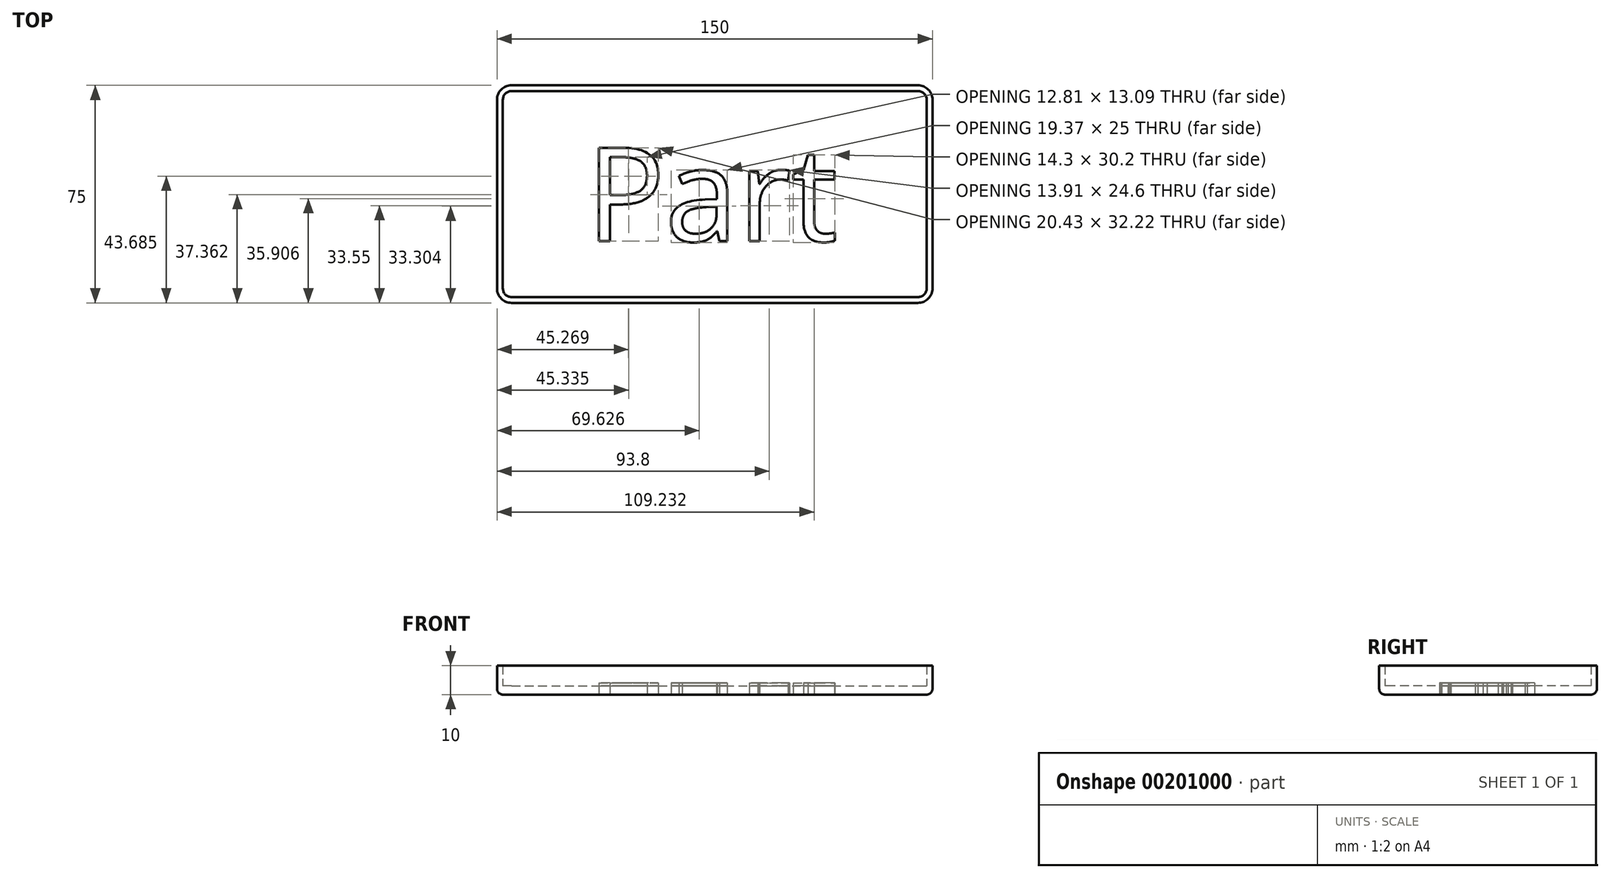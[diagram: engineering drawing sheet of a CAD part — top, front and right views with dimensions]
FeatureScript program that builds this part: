
annotation { "Feature Type Name" : "Feature", "Feature Type Description" : "" }
export const myFeature = defineFeature(function(context is Context, id is Id, definition is map)
    precondition{}
    {
        {
            var Q0;
            Q0=qCreatedBy(makeId("Top.planeOp"),FACE);
            var sketch = newSketch(context, id + "F0", { "sketchPlane" : qUnion([Q0])});
            skLineSegment(sketch, "E0.bottom", {"start": v(-41.61, 75) * mm, "end": v(98.39, 75) * mm});
            skLineSegment(sketch, "E0.top", {"start": v(-41.61, 0) * mm, "end": v(98.39, 0) * mm});
            skLineSegment(sketch, "E0.left", {"start": v(-46.61, 70) * mm, "end": v(-46.61, 5) * mm});
            skLineSegment(sketch, "E0.right", {"start": v(103.39, 70) * mm, "end": v(103.39, 5) * mm});
            skLineSegment(sketch, "E1.0", {"start": v(-41.61, 2) * mm, "end": v(98.39, 2) * mm});
            skLineSegment(sketch, "E1.1", {"start": v(-44.61, 70) * mm, "end": v(-44.61, 5) * mm});
            skLineSegment(sketch, "E1.2", {"start": v(-41.61, 73) * mm, "end": v(98.39, 73) * mm});
            skLineSegment(sketch, "E1.3", {"start": v(101.39, 70) * mm, "end": v(101.39, 5) * mm});
            skLineSegment(sketch, "E2", {"start": v(28.39, 73) * mm, "end": v(28.39, 2) * mm, "construction": true});
            skText(sketch, "E3", { "text": "Part", "fontName": "OpenSans-Regular.ttf"});
            skLineSegment(sketch, "E4", {"start": v(72.7, 37.5) * mm, "end": v(-15.92, 37.5) * mm, "construction": true});
            skLineSegment(sketch, "E5", {"start": v(28.39, 37.5) * mm, "end": v(101.39, 37.5) * mm, "construction": true});
            skPoint(sketch, "E6.visualSharp", {"position": v(101.39, 73) * mm});
            skArc(sketch, "E6.filletArc", {"start": v(101.39, 70) * mm, "mid": v(100.5, 72.12) * mm, "end": v(98.39, 73) * mm});
            skPoint(sketch, "E7.visualSharp", {"position": v(-44.61, 73) * mm});
            skArc(sketch, "E7.filletArc", {"start": v(-41.61, 73) * mm, "mid": v(-43.73, 72.12) * mm, "end": v(-44.61, 70) * mm});
            skPoint(sketch, "E8.visualSharp", {"position": v(-44.61, 2) * mm});
            skArc(sketch, "E8.filletArc", {"start": v(-44.61, 5) * mm, "mid": v(-43.73, 2.88) * mm, "end": v(-41.61, 2) * mm});
            skPoint(sketch, "E9.visualSharp", {"position": v(101.39, 2) * mm});
            skArc(sketch, "E9.filletArc", {"start": v(98.39, 2) * mm, "mid": v(100.5, 2.88) * mm, "end": v(101.39, 5) * mm});
            skPoint(sketch, "E10.visualSharp", {"position": v(103.39, 0) * mm});
            skArc(sketch, "E10.filletArc", {"start": v(98.39, 0) * mm, "mid": v(101.92, 1.46) * mm, "end": v(103.39, 5) * mm});
            skPoint(sketch, "E11.visualSharp", {"position": v(103.39, 75) * mm});
            skArc(sketch, "E11.filletArc", {"start": v(103.39, 70) * mm, "mid": v(101.92, 73.54) * mm, "end": v(98.39, 75) * mm});
            skPoint(sketch, "E12.visualSharp", {"position": v(-46.61, 75) * mm});
            skArc(sketch, "E12.filletArc", {"start": v(-41.61, 75) * mm, "mid": v(-45.15, 73.54) * mm, "end": v(-46.61, 70) * mm});
            skPoint(sketch, "E13.visualSharp", {"position": v(-46.61, 0) * mm});
            skArc(sketch, "E13.filletArc", {"start": v(-46.61, 5) * mm, "mid": v(-45.15, 1.46) * mm, "end": v(-41.61, 0) * mm});
            const initialGuessF0  = {"E3": [-0.01592, 0.02125, 1, 0, 0.0325]};
            skSetInitialGuess(sketch, initialGuessF0);
            skSolve(sketch);
        }
        {
            var Q0;
            Q0=makeQuery(id+"F0.imprint","IMPRINT",FACE,{"disambiguationData":[TD([[makeQuery(id+"F0.imprint","IMPRINT",EDGE,{"derivedFrom":sQuery(id+"F0.wireOp",EDGE,"E1.0")}),1.0]])]});
            var Q1;
            Q1=makeQuery(id+"F0.imprint","IMPRINT",FACE,{"disambiguationData":[TD([[makeQuery(id+"F0.imprint","IMPRINT",EDGE,{"derivedFrom":sQuery(id+"F0.wireOp",EDGE,"E3.sketch_text.stroke-63")}),1.0]])]});
            var Q2;
            Q2=makeQuery(id+"F0.imprint","IMPRINT",FACE,{"disambiguationData":[TD([[makeQuery(id+"F0.imprint","IMPRINT",EDGE,{"derivedFrom":sQuery(id+"F0.wireOp",EDGE,"E3.sketch_text.stroke-17")}),1.0]])]});
            var Q3;
            Q3=makeQuery(id+"F0.imprint","IMPRINT",FACE,{"disambiguationData":[TD([[makeQuery(id+"F0.imprint","IMPRINT",EDGE,{"derivedFrom":sQuery(id+"F0.wireOp",EDGE,"E3.sketch_text.stroke-34")}),1.0]])]});
            var Q4;
            Q4=makeQuery(id+"F0.imprint","IMPRINT",FACE,{"disambiguationData":[TD([[makeQuery(id+"F0.imprint","IMPRINT",EDGE,{"derivedFrom":sQuery(id+"F0.wireOp",EDGE,"E3.sketch_text.stroke-8")}),1.0]])]});
            extrude(context, id + "F1", {"entities" : qUnion([Q0, Q1, Q2, Q3, Q4]), "depth" : 3 * mm});
        }
        {
            var Q0;
            Q0=makeQuery(id+"F0.imprint","IMPRINT",FACE,{"disambiguationData":[TD([[makeQuery(id+"F0.imprint","IMPRINT",EDGE,{"derivedFrom":sQuery(id+"F0.wireOp",EDGE,"E0.bottom")}),-1.0]])]});
            extrude(context, id + "F2", {"entities" : qUnion([Q0]), "operationType" : NewBodyOperationType.ADD, "depth" : 10 * mm});
        }
        {
            var Q0;
            Q0=makeQuery(id+"F0.imprint","IMPRINT",FACE,{"disambiguationData":[TD([[makeQuery(id+"F0.imprint","IMPRINT",EDGE,{"derivedFrom":sQuery(id+"F0.wireOp",EDGE,"E3.sketch_text.stroke-0")}),-1.0]])]});
            var Q1;
            Q1=makeQuery(id+"F0.imprint","IMPRINT",FACE,{"disambiguationData":[TD([[makeQuery(id+"F0.imprint","IMPRINT",EDGE,{"derivedFrom":sQuery(id+"F0.wireOp",EDGE,"E3.sketch_text.stroke-8")}),-1.0]])]});
            var Q2;
            Q2=makeQuery(id+"F0.imprint","IMPRINT",FACE,{"disambiguationData":[TD([[makeQuery(id+"F0.imprint","IMPRINT",EDGE,{"derivedFrom":sQuery(id+"F0.wireOp",EDGE,"E3.sketch_text.stroke-25")}),-1.0]])]});
            var Q3;
            Q3=makeQuery(id+"F0.imprint","IMPRINT",FACE,{"disambiguationData":[TD([[makeQuery(id+"F0.imprint","IMPRINT",EDGE,{"derivedFrom":sQuery(id+"F0.wireOp",EDGE,"E3.sketch_text.stroke-44")}),-1.0]])]});
            var Q4;
            Q4=makeQuery(id+"F0.imprint","IMPRINT",FACE,{"disambiguationData":[TD([[makeQuery(id+"F0.imprint","IMPRINT",EDGE,{"derivedFrom":sQuery(id+"F0.wireOp",EDGE,"E3.sketch_text.stroke-71")}),-1.0]])]});
            extrude(context, id + "F3", {"entities" : qUnion([Q0, Q1, Q2, Q3, Q4]), "depth" : 4 * mm});
        }
        {
            var Q0;
            Q0=makeQuery(id+"F2.opExtrude","CAP_EDGE",EDGE,{"disambiguationData":[OSD([sQuery(id+"F0.wireOp",EDGE,"E0.right")])],"isStart":true});
            fillet(context, id + "F4", {"entities" : qUnion([Q0]), "radius" : 2 * mm, "tangentPropagation" : true, "allowEdgeOverflow" : false});
        }
    });
